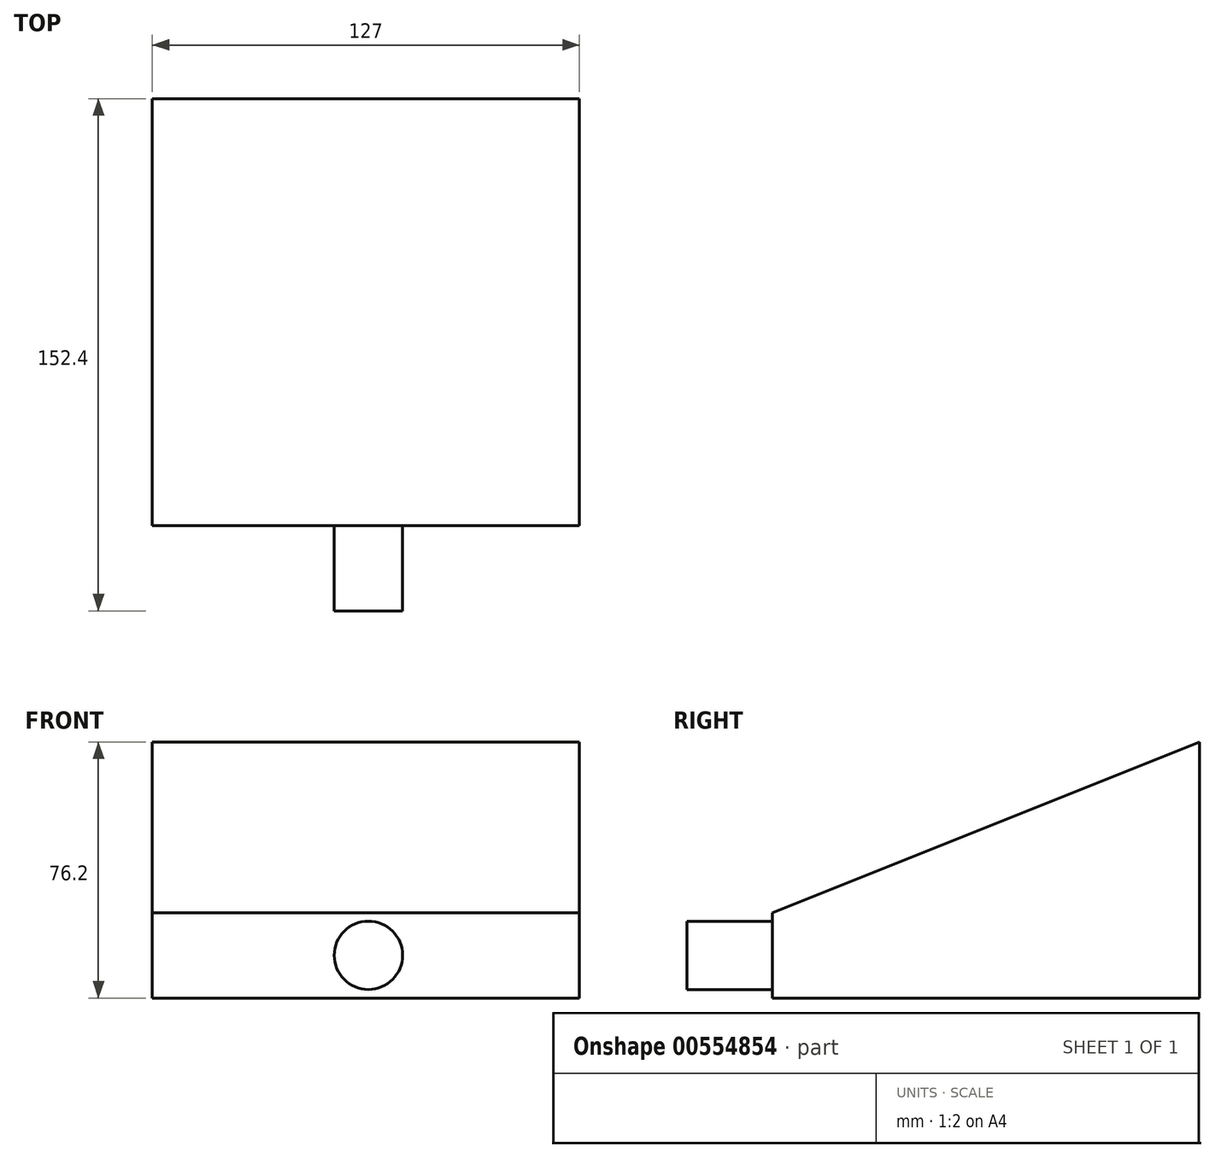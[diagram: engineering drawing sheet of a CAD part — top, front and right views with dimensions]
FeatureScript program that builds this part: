
annotation { "Feature Type Name" : "Feature", "Feature Type Description" : "" }
export const myFeature = defineFeature(function(context is Context, id is Id, definition is map)
    precondition{}
    {
        {
            var Q0;
            Q0=qCreatedBy(makeId("Right.planeOp"),FACE);
            var sketch = newSketch(context, id + "F0", { "sketchPlane" : qUnion([Q0])});
            skLineSegment(sketch, "E0.bottom", {"start": v(0, 12.7) * mm, "end": v(127, 12.7) * mm});
            skLineSegment(sketch, "E0.top", {"start": v(0, -12.7) * mm, "end": v(127, -12.7) * mm});
            skLineSegment(sketch, "E0.left", {"start": v(0, 12.7) * mm, "end": v(0, -12.7) * mm});
            skLineSegment(sketch, "E0.right", {"start": v(127, 12.7) * mm, "end": v(127, -12.7) * mm});
            skLineSegment(sketch, "E1", {"start": v(0, 12.7) * mm, "end": v(127, 63.5) * mm});
            skLineSegment(sketch, "E2", {"start": v(127, 63.5) * mm, "end": v(127, 12.7) * mm});
            skLineSegment(sketch, "E3.bottom", {"start": v(0, 12.7) * mm, "end": v(12.85, 12.7) * mm});
            skLineSegment(sketch, "E3.top", {"start": v(0, -12.7) * mm, "end": v(12.85, -12.7) * mm});
            skLineSegment(sketch, "E3.right", {"start": v(12.85, 12.7) * mm, "end": v(12.85, -12.7) * mm});
            skLineSegment(sketch, "E4.left", {"start": v(0, -12.7) * mm, "end": v(0, 0) * mm});
            skSolve(sketch);
        }
        {
            var Q0;
            Q0=makeQuery(id+"F0.imprint","IMPRINT",FACE,{"disambiguationData":[TD([[makeQuery(id+"F0.imprint","IMPRINT",EDGE,{"derivedFrom":sQuery(id+"F0.wireOp",EDGE,"E0.bottom")}),1.0]])]});
            var Q1;
            Q1=makeQuery(id+"F0.imprint","IMPRINT",FACE,{"disambiguationData":[TD([[makeQuery(id+"F0.imprint","IMPRINT",EDGE,{"derivedFrom":sQuery(id+"F0.wireOp",EDGE,"E0.bottom")}),-1.0]])]});
            var Q2;
            Q2=makeQuery(id+"F0.imprint","IMPRINT",FACE,{"disambiguationData":[TD([[makeQuery(id+"F0.imprint","IMPRINT",EDGE,{"derivedFrom":sQuery(id+"F0.wireOp",EDGE,"E3.bottom")}),-1.0]])]});
            var Q3;
            Q3 = qSketchRegion(id + "F2", true);
            extrude(context, id + "F1", {"entities" : qUnion([Q0, Q1, Q2, Q3]), "depth" : 127 * mm, "offsetDistance" : 25.4 * mm});
        }
        {
            var Q0;
            Q0=makeQuery(id+"F1.opExtrude","SWEPT_FACE",FACE,{"disambiguationData":[OSD([sQuery(id+"F0.wireOp",EDGE,"E0.left"),sQuery(id+"F0.wireOp",EDGE,"E4.left")])]});
            var sketch = newSketch(context, id + "F2", { "sketchPlane" : qUnion([Q0])});
            skCircle(sketch, "E5", {"center": v(64.25, 0) * mm, "radius": 10.16 * mm});
            skSolve(sketch);
        }
        {
            var Q0;
            Q0 = qSketchRegion(id + "F2", true);
            extrude(context, id + "F3", {"entities" : qUnion([Q0]), "operationType" : NewBodyOperationType.ADD, "depth" : 25.4 * mm, "offsetDistance" : 25.4 * mm});
        }
    });
